# Revit family: SD 6060 PPL
name_source: partatom
category: Lighting Fixtures
revit_build: Autodesk Revit 2017 (Build: 20160225_1515(x64)
units: mm (PartAtom-declared; Revit-internal decimal feet)

## family parameters
Cut with Voids When Loaded = No
Host = Face
Light Source = Yes
Part Type = Normal
Room Calculation Point = No
Round Connector Dimension = Use Diameter
Shared = No

## types (4) — shared parameters
Color Filter = 16777215
Default Elevation = 1219 mm
Dimming Lamp Color Temperature Shift = <None>
Emit Shape Visible in Rendering = Yes
Emit from Rectangle Length = 500 mm  [stored 1.64042 ft]
Emit from Rectangle Width = 500 mm  [stored 1.64042 ft]
Manufacturer = ARLIGHT
Model = SD6060PPL
Tilt Angle = 90.00°
Type Comments = Surface Mounted
Type Image = <None>

## per-type parameters (varying)
| type | Apparent Load | Photometric Web File | Wattage Comments |
| SDPPL.6060.20.40 | 20 VA | sd-6060-ppl-20w-4k-sa.ies | 20W |
| SDPPL.6060.27.40 | 27 VA | sd-6060-ppl-27w-4k-sa.ies | 27W |
| SDPPL.6060.36.40 | 36 VA | sd-6060-ppl-36w-4k-sa.ies | 36W |
| SDPPL.6060.42.40 | 42 VA | sd-6060-ppl-42w-4k-sa.ies | 42W |

note: [stored X ft] marks values corroborated as IEEE doubles in the binary element streams (Revit-internal decimal feet)

## geometry (parser evidence)
native form markers: Sweep x1
no freeform markers — native parametric forms only
